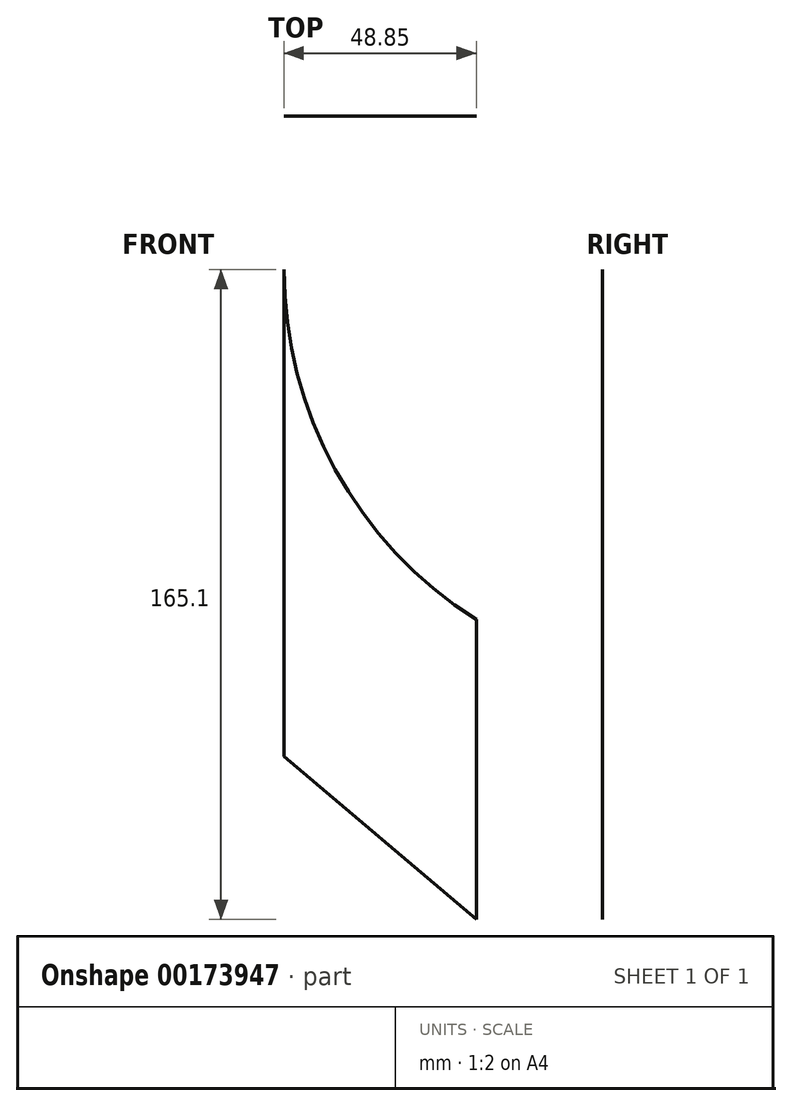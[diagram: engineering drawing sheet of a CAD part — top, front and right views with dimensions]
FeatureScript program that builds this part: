
annotation { "Feature Type Name" : "Feature", "Feature Type Description" : "" }
export const myFeature = defineFeature(function(context is Context, id is Id, definition is map)
    precondition{}
    {
        {
            var Q0;
            Q0=qCreatedBy(makeId("Front.planeOp"),FACE);
            var sketch = newSketch(context, id + "F0", { "sketchPlane" : qUnion([Q0])});
            skLineSegment(sketch, "E0", {"start": v(0, 57.78) * mm, "end": v(0, -65.97) * mm});
            skLineSegment(sketch, "E1", {"start": v(0, -65.97) * mm, "end": v(48.85, -65.97) * mm});
            skLineSegment(sketch, "E2", {"start": v(48.85, -65.97) * mm, "end": v(48.85, -31.16) * mm});
            skLineSegment(sketch, "E3", {"start": v(48.85, -31.16) * mm, "end": v(48.85, -65.97) * mm});
            skLineSegment(sketch, "E4", {"start": v(48.85, -65.97) * mm, "end": v(48.85, -107.32) * mm});
            skPoint(sketch, "E4.endSnap0", {"position": v(48.85, -48.56) * mm});
            skLineSegment(sketch, "E5", {"start": v(48.85, -107.32) * mm, "end": v(0, -65.97) * mm});
            skArc(sketch, "E6", {"start": v(0, 57.78) * mm, "mid": v(13.02, 7.04) * mm, "end": v(48.85, -31.16) * mm});
            skSolve(sketch);
        }
        {
            var Q0;
            Q0 = qSketchRegion(id + "F0", true);
            extrude(context, id + "F1", {"entities" : qUnion([Q0]), "depth" : 1 / 406.4 * mm});
        }
    });
